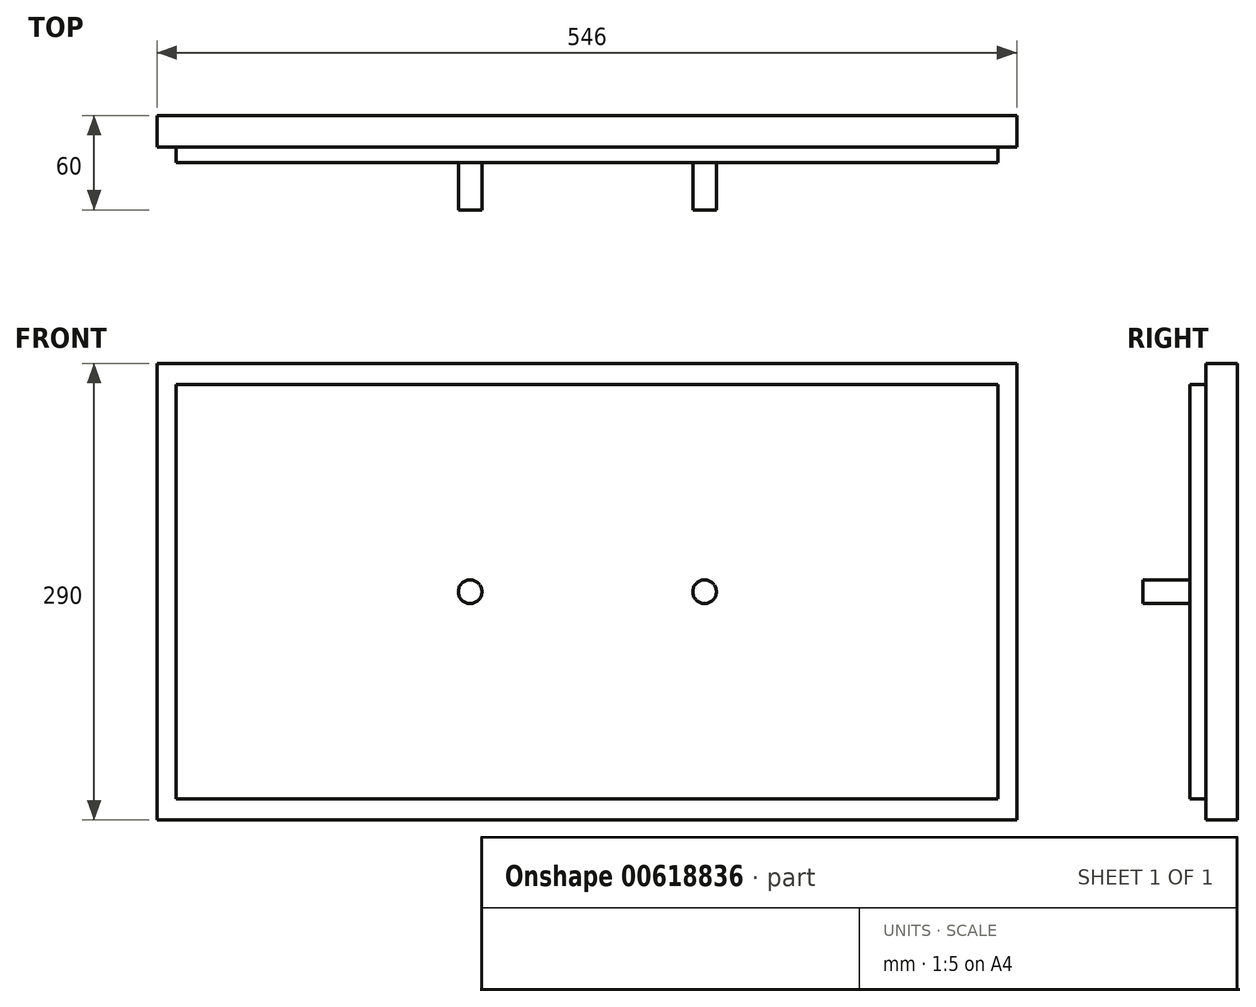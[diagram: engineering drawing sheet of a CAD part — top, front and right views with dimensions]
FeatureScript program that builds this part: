
annotation { "Feature Type Name" : "Feature", "Feature Type Description" : "" }
export const myFeature = defineFeature(function(context is Context, id is Id, definition is map)
    precondition{}
    {
        {
            var Q0;
            Q0=qCreatedBy(makeId("Front.planeOp"),FACE);
            var sketch = newSketch(context, id + "F0", { "sketchPlane" : qUnion([Q0])});
            skLineSegment(sketch, "E0.bottom", {"start": v(-273, 145) * mm, "end": v(273, 145) * mm});
            skLineSegment(sketch, "E0.top", {"start": v(-273, -145) * mm, "end": v(273, -145) * mm});
            skLineSegment(sketch, "E0.left", {"start": v(-273, 145) * mm, "end": v(-273, -145) * mm});
            skLineSegment(sketch, "E0.right", {"start": v(273, 145) * mm, "end": v(273, -145) * mm});
            skPoint(sketch, "E0.middle", {"position": v(0, 0) * mm});
            skSolve(sketch);
        }
        {
            var Q0;
            Q0 = qSketchRegion(id + "F0", true);
            extrude(context, id + "F1", {"entities" : qUnion([Q0]), "depth" : 20 * mm, "offsetDistance" : 25 * mm});
        }
        {
            var Q0;
            Q0=makeQuery(id+"F1.opExtrude","CAP_FACE",FACE,{"disambiguationData":[OSD([sQuery(id+"F0.wireOp",EDGE,"E0.bottom"),sQuery(id+"F0.wireOp",EDGE,"E0.top"),sQuery(id+"F0.wireOp",EDGE,"E0.left"),sQuery(id+"F0.wireOp",EDGE,"E0.right")])],"isStart":false});
            var sketch = newSketch(context, id + "F2", { "sketchPlane" : qUnion([Q0])});
            skLineSegment(sketch, "E1.bottom", {"start": v(-260.98, 131.5) * mm, "end": v(260.98, 131.5) * mm});
            skLineSegment(sketch, "E1.top", {"start": v(-260.98, -131.5) * mm, "end": v(260.98, -131.5) * mm});
            skLineSegment(sketch, "E1.left", {"start": v(-260.98, 131.5) * mm, "end": v(-260.98, -131.5) * mm});
            skLineSegment(sketch, "E1.right", {"start": v(260.98, 131.5) * mm, "end": v(260.98, -131.5) * mm});
            skPoint(sketch, "E1.middle", {"position": v(0, 0) * mm});
            skSolve(sketch);
        }
        {
            var Q0;
            Q0=makeQuery(id+"F2.imprint","IMPRINT",FACE,{"disambiguationData":[TD([[makeQuery(id+"F2.imprint","IMPRINT",EDGE,{"derivedFrom":sQuery(id+"F2.wireOp",EDGE,"E1.bottom")}),-1.0]])]});
            extrude(context, id + "F3", {"entities" : qUnion([Q0]), "operationType" : NewBodyOperationType.ADD, "depth" : 10 * mm, "offsetDistance" : 25 * mm});
        }
        {
            var Q0;
            Q0=makeQuery(id+"F3.opExtrude","CAP_FACE",FACE,{"disambiguationData":[OSD([sQuery(id+"F2.wireOp",EDGE,"E1.bottom"),sQuery(id+"F2.wireOp",EDGE,"E1.top"),sQuery(id+"F2.wireOp",EDGE,"E1.left"),sQuery(id+"F2.wireOp",EDGE,"E1.right")])],"isStart":false});
            var sketch = newSketch(context, id + "F4", { "sketchPlane" : qUnion([Q0])});
            skCircle(sketch, "E2", {"center": v(-74.2, 0) * mm, "radius": 7.5 * mm});
            skCircle(sketch, "E3", {"center": v(74.72, 0) * mm, "radius": 7.5 * mm});
            skSolve(sketch);
        }
        {
            var Q0;
            Q0 = qSketchRegion(id + "F4", true);
            extrude(context, id + "F5", {"entities" : qUnion([Q0]), "operationType" : NewBodyOperationType.ADD, "depth" : 30 * mm, "offsetDistance" : 25 * mm});
        }
    });
